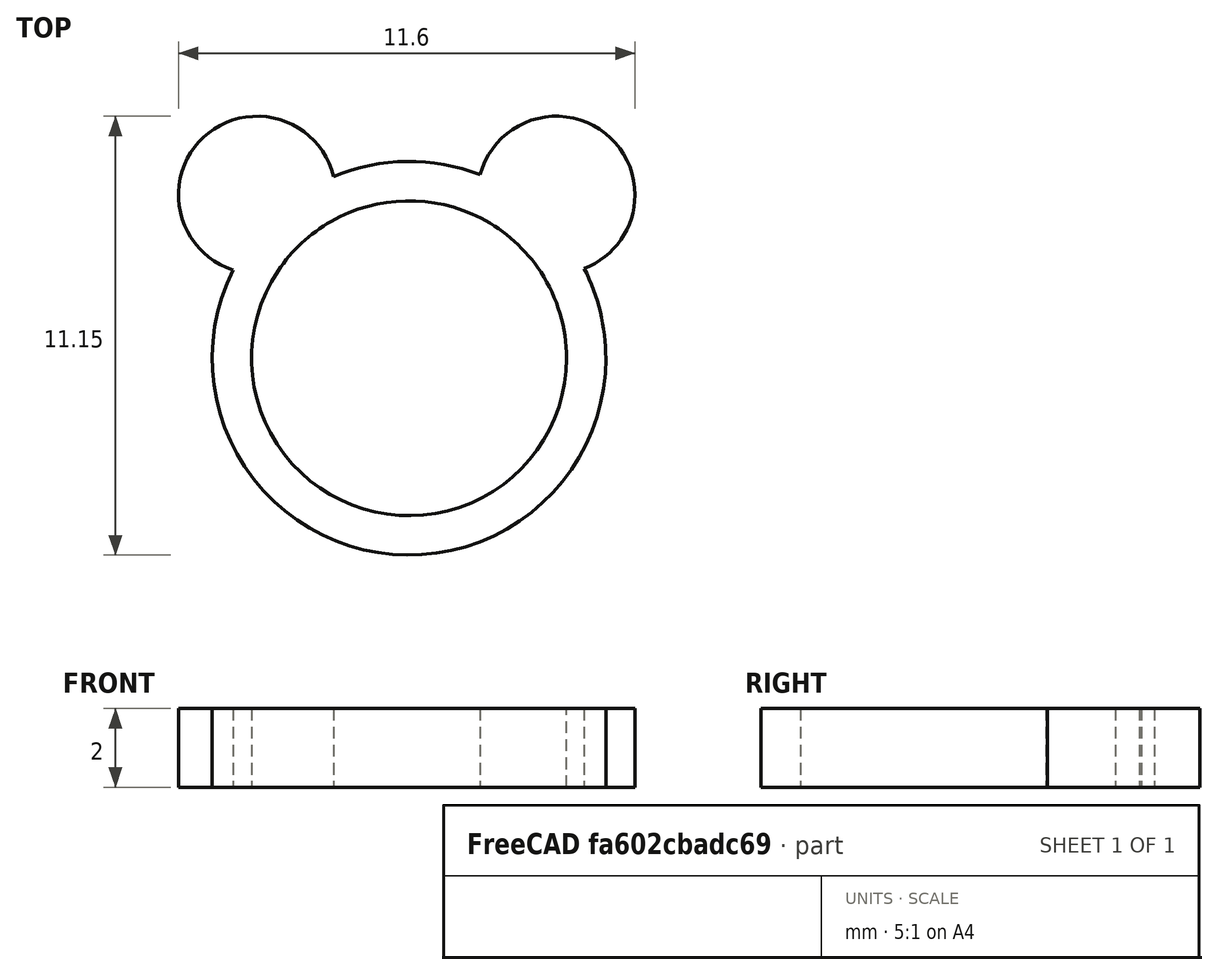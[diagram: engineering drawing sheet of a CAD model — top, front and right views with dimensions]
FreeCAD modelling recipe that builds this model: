
FCSTD DOCUMENT  (FreeCAD 0.20R29410 (Git))
Label: Anillo
License: Creative Commons Attribution-NonCommercial-ShareAlike
LicenseURL: http://creativecommons.org/licenses/by-nc-sa/4.0/
objects: Part::Cylinder×4, Part::Cut×2, Part::Fuse×1, Part::MultiFuse×1
note: 8 computed .brp shape members not serialized (recipe doc carries the construction recipe); baked Part::Feature solids carry a one-line shape summary decoded from their .brp

FEATURE [Part::Cylinder] Cylinder  label="Exterior"
  Angle = 360
  AttacherType = Attacher::AttachEngine3D
  FirstAngle = 0
  Height = 2
  Radius = 5
  SecondAngle = 0
FEATURE [Part::Cylinder] Cylinder001  label="Interior"
  Angle = 360
  AttacherType = Attacher::AttachEngine3D
  FirstAngle = 0
  Height = 5
  Placement = pos=(0,0,-1.53) rot=(0,0,1;0rad)
  Radius = 4
  SecondAngle = 0
FEATURE [Part::Cut] Cut
  Base = -> Cylinder
  Tool = -> Cylinder001
FEATURE [Part::Cylinder] Cylinder002  label="Oreja"
  Angle = 360
  AttacherType = Attacher::AttachEngine3D
  FirstAngle = 0
  Height = 2
  Placement = pos=(-3.86,4.15,0) rot=(0,0,1;0rad)
  Radius = 2
  SecondAngle = 0
FEATURE [Part::Cylinder] Cylinder003  label="Oreja001"
  Angle = 360
  AttacherType = Attacher::AttachEngine3D
  FirstAngle = 0
  Height = 2
  Placement = pos=(3.74,4.15,0) rot=(0,0,1;0rad)
  Radius = 2
  SecondAngle = 0
FEATURE [Part::Fuse] Fusion
  Base = -> Cylinder002
  Tool = -> Cylinder003
FEATURE [Part::Cut] Cut001
  Base = -> Fusion
  Tool = -> Cylinder001
FEATURE [Part::MultiFuse] Fusion001
  Shapes = -> [Cut,Cut001]
